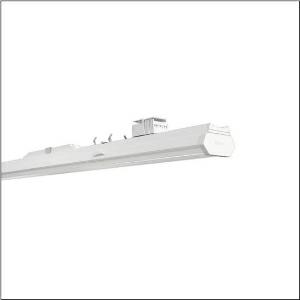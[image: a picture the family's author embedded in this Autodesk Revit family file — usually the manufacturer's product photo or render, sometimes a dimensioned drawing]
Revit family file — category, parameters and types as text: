
# Revit family: licross_r__11_protected_mo_51td11mn495g_5082
name_source: partatom
category: Lighting Fixtures
units: mm (PartAtom-declared; Revit-internal decimal feet)

## family parameters
Cut with Voids When Loaded = No
Host = Face
Light Source = No
Part Type = Normal
Room Calculation Point = No
Round Connector Dimension = Use Diameter
Shared = No

## types (1)
- --- (1 x LED, 9980 lm, 55.3 W, 4000K)
    Apparent Load = 55 VA
    CIE Flux Codes = 83 94 98 100 100
    Color Rendering = 80
    Color Temperature = 4000K
    Default Elevation = 1800 mm
    Description = Licross® 11 Protected MO, luminaire insert, of sheet steel, galvanised, coil coated, white, length: 1.500mm, width: 90mm, height: 101mm, LED rated luminous flux: 9.980lm, light colour: 840, control gear: ON/OFF Multilumen, control gear: ECG Multilumen, with plug, 3-pole, with phase selection, mains connection: 220..240V, AC, 50/60Hz, halogen-free wiring, primary light control with lens, of plastic, primary optical cover: cover, of PMMA, light emission: direct with ceiling illumination distribution, primary light characteristic: symmetric, protection rating (complete): IP54, insulation class (complete): insulation class I (protective earthing), certification: CE, ENEC, VDE, UKCA, protection symbol: D if used in an environment with non-conductive dust loads with corresponding accessories, impact resistance: IK06, permissible ambient temperature for indoor applications: -35..+40°C, corresponds to IFS (International Featured Standards) requirements for safety and quality in the food industry, reducing of maximum allowable ambient temperature of 5°C with ceiling mounting, LABS conformity tested according to VDMA 24364:2018-05, packaging unit: 1 piece
    Height = 92 mm
    Lamp = 1 x LED
    Lamp Light Flux = 9980 lm
    Lamp Power = 55.3 W
    Lamp count = 1
    Length = 1500 mm
    Luminous efficacy = 180 lm/W
    Manufacturer = Siteco
    ModVariant = No
    Model = 51TD11MN495G
    Mounting Place = Ceiling
    Mounting Type = Pendant
    Number of Poles = 1
    OnlyDefault = Yes
    Power Factor = 1
    Product Name = Licross® 11 Protected MO
    Product group = luminaire insert
    ProductGroupID = 902
    Protection Class = Protection class I
    Protection Degree = IP 54
    RLX_Detail_Level = 1
    RlxData = <blob elided: 21785 chars, md5=943c1623>
    Socket = socket
    Standby Power = 0 W
    System Light Flux = 9980 lm
    System Power = 55 W
    Type Comments = factory setting: luminous flux: 100 % | (A | C | E) | 126 mA
    Type Image = l_1256145.jpg
    URL = http://relux.com
    VarID = @adj_003739
    Voltage = 0 V
    Weight = 0.00 kg
    Width = 88 mm

## geometry (parser evidence)
native form markers: Blend x4, Sweep x13
no freeform markers — native parametric forms only
